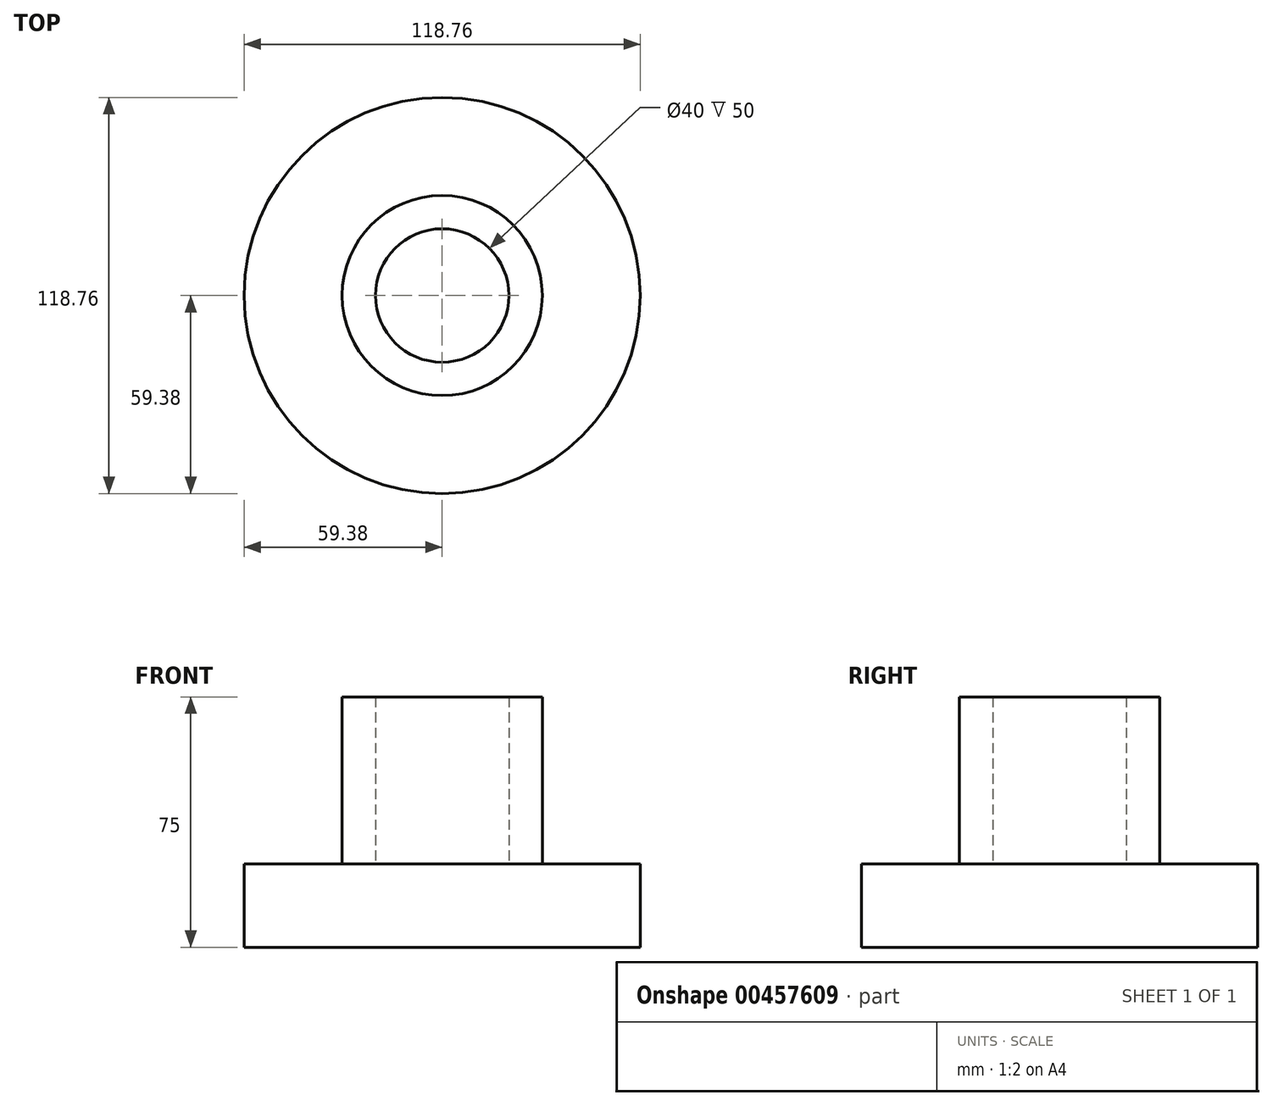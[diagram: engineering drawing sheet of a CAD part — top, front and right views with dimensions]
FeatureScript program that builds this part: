
annotation { "Feature Type Name" : "Feature", "Feature Type Description" : "" }
export const myFeature = defineFeature(function(context is Context, id is Id, definition is map)
    precondition{}
    {
        {
            var Q0;
            Q0=qCreatedBy(makeId("Top.planeOp"),FACE);
            var sketch = newSketch(context, id + "F0", { "sketchPlane" : qUnion([Q0])});
            skCircle(sketch, "E0", {"center": v(0, 0) * mm, "radius": 30 * mm});
            skSolve(sketch);
        }
        {
            var Q0;
            Q0=makeQuery(id+"F0.imprint","IMPRINT",FACE,{"disambiguationData":[TD([[makeQuery(id+"F0.imprint","IMPRINT",EDGE,{"derivedFrom":sQuery(id+"F0.wireOp",EDGE,"E0")}),1.0]])]});
            extrude(context, id + "F1", {"entities" : qUnion([Q0]), "depth" : 75 * mm});
        }
        {
            var Q0;
            Q0=qCreatedBy(makeId("Top.planeOp"),FACE);
            var sketch = newSketch(context, id + "F2", { "sketchPlane" : qUnion([Q0])});
            skCircle(sketch, "E1", {"center": v(0, 0) * mm, "radius": 20 * mm});
            skSolve(sketch);
        }
        {
            var Q0;
            Q0 = qSketchRegion(id + "F2", true);
            var Q1;
            Q1=makeQuery(id+"F1.opExtrude","CAP_FACE",FACE,{"disambiguationData":[OSD([sQuery(id+"F0.wireOp",EDGE,"E0")])],"isStart":false});
            extrude(context, id + "F3", {"entities" : qUnion([Q0]), "operationType" : NewBodyOperationType.REMOVE, "endBound" : BoundingType.UP_TO_SURFACE, "endBoundEntityFace" : qUnion([Q1]), "depth" : 25 * mm});
        }
        {
            var Q0;
            Q0=qCreatedBy(makeId("Top.planeOp"),FACE);
            var sketch = newSketch(context, id + "F4", { "sketchPlane" : qUnion([Q0])});
            skCircle(sketch, "E2", {"center": v(0, 0) * mm, "radius": 59.38 * mm});
            skSolve(sketch);
        }
        {
            var Q0;
            Q0 = qSketchRegion(id + "F4", true);
            extrude(context, id + "F5", {"entities" : qUnion([Q0]), "operationType" : NewBodyOperationType.ADD, "depth" : 25 * mm});
        }
    });
